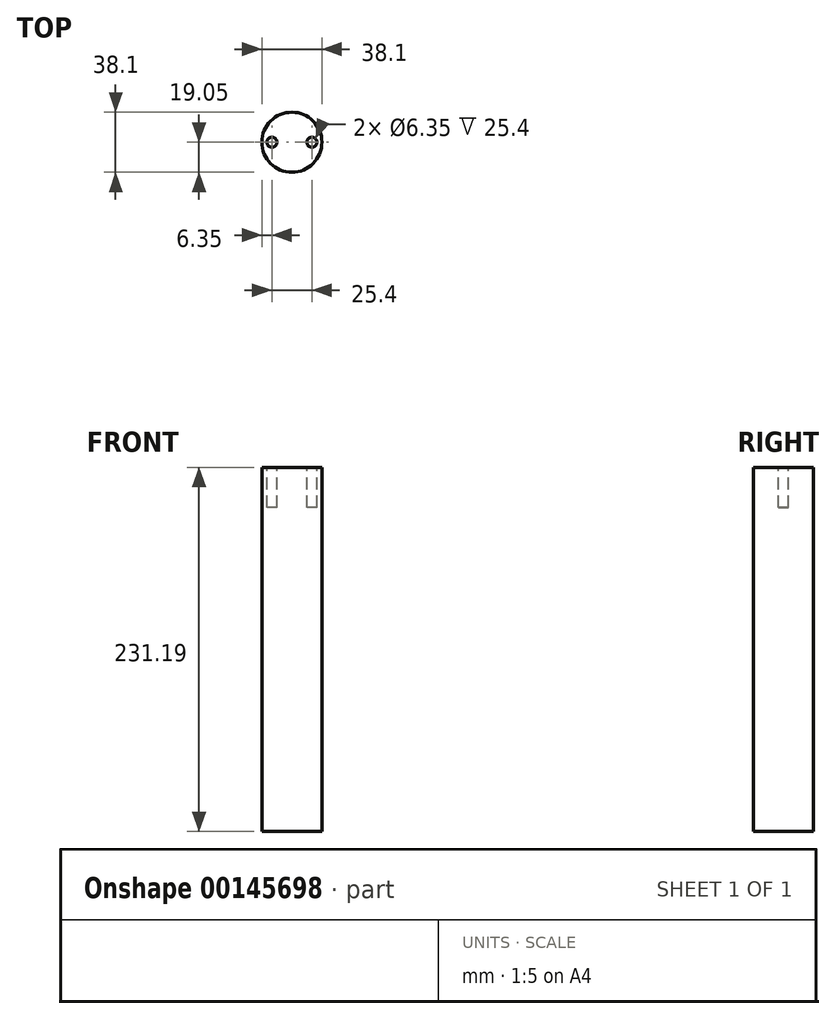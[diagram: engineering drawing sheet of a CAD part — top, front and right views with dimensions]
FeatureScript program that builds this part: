
annotation { "Feature Type Name" : "Feature", "Feature Type Description" : "" }
export const myFeature = defineFeature(function(context is Context, id is Id, definition is map)
    precondition{}
    {
        {
            var Q0;
            Q0=qCreatedBy(makeId("Top.planeOp"),FACE);
            var sketch = newSketch(context, id + "F0", { "sketchPlane" : qUnion([Q0])});
            skCircle(sketch, "E0", {"center": v(0, 0) * mm, "radius": 19.05 * mm});
            skSolve(sketch);
        }
        {
            var Q0;
            Q0 = qSketchRegion(id + "F0", true);
            extrude(context, id + "F1", {"entities" : qUnion([Q0]), "depth" : 231.2 * mm});
        }
        {
            var Q0;
            Q0=makeQuery(id+"F1.opExtrude","CAP_FACE",FACE,{"disambiguationData":[OSD([sQuery(id+"F0.wireOp",EDGE,"E0")])],"isStart":false});
            var sketch = newSketch(context, id + "F2", { "sketchPlane" : qUnion([Q0])});
            skLineSegment(sketch, "E1", {"start": v(-19.05, 0) * mm, "end": v(19.05, 0) * mm});
            skSolve(sketch);
        }
        {
            var Q0;
            {var subQ0=sQuery(id+"F2.wireOp",EDGE,"E1");Q0=makeQuery(id+"F2.imprint","IMPRINT",FACE,{"disambiguationData":[TD([[makeQuery(id+"F2.imprint","IMPRINT",EDGE,{"derivedFrom":subQ0}),1.0]])]});}
            var sketch = newSketch(context, id + "F3", { "sketchPlane" : qUnion([Q0])});
            skCircle(sketch, "E2", {"center": v(-12.7, 0) * mm, "radius": 3.18 * mm});
            skCircle(sketch, "E3", {"center": v(12.7, 0) * mm, "radius": 3.18 * mm});
            skSolve(sketch);
        }
        {
            var Q0;
            Q0 = qSketchRegion(id + "F3", true);
            extrude(context, id + "F4", {"entities" : qUnion([Q0]), "operationType" : NewBodyOperationType.REMOVE, "oppositeDirection" : true, "depth" : 25.4 * mm});
        }
    });
